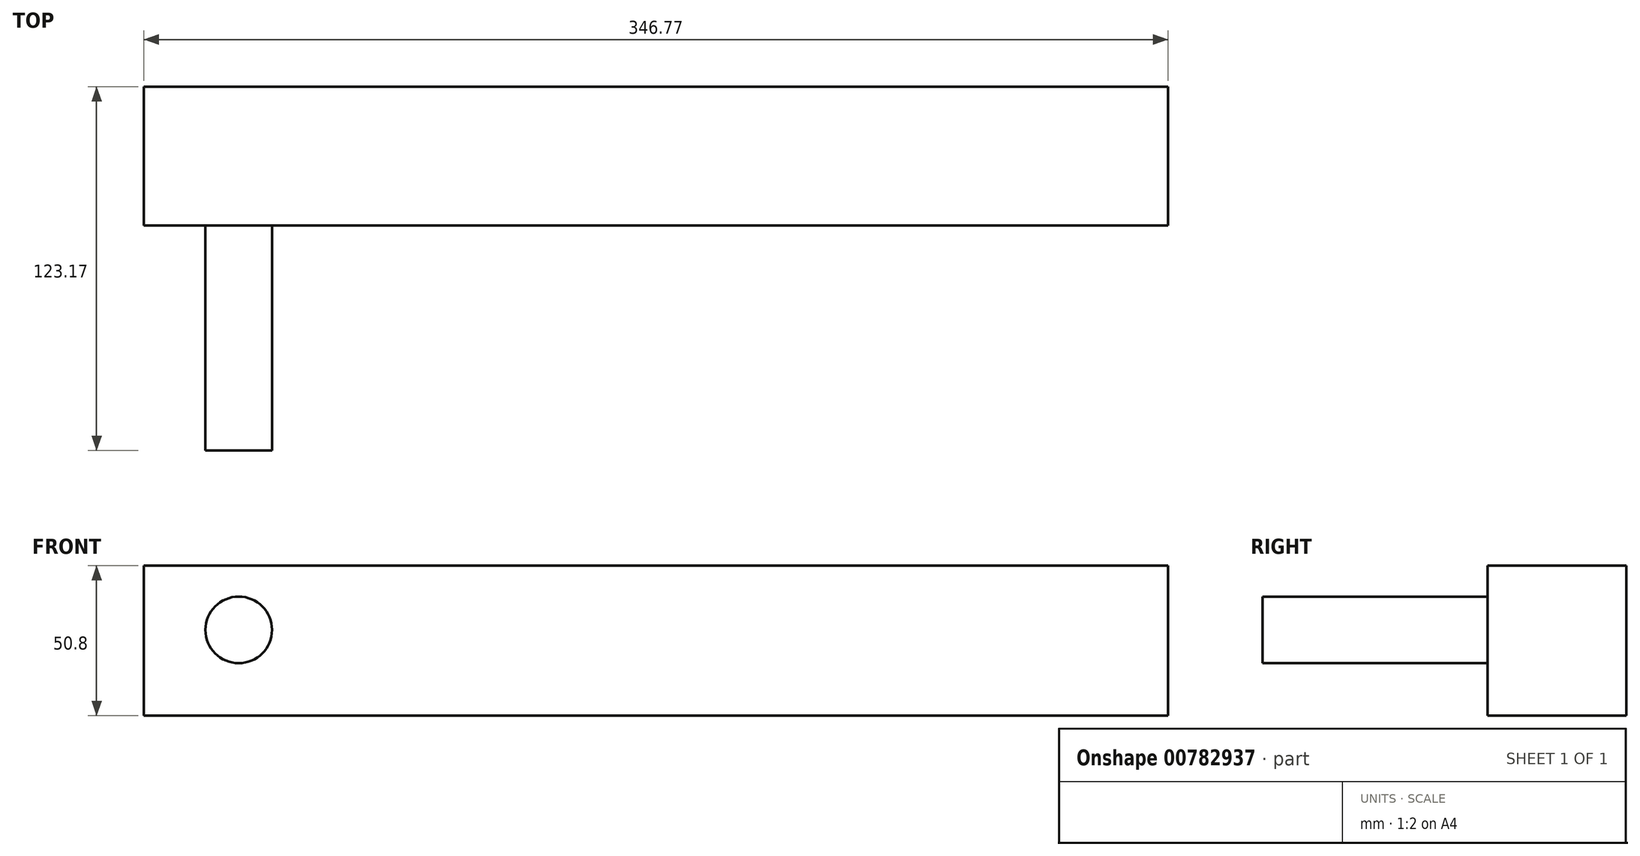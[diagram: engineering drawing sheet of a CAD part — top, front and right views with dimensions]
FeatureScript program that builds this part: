
annotation { "Feature Type Name" : "Feature", "Feature Type Description" : "" }
export const myFeature = defineFeature(function(context is Context, id is Id, definition is map)
    precondition{}
    {
        {
            var Q0;
            Q0=qCreatedBy(makeId("Top.planeOp"),FACE);
            var sketch = newSketch(context, id + "F0", { "sketchPlane" : qUnion([Q0])});
            skLineSegment(sketch, "E0.bottom", {"start": v(-140.56, 22.3) * mm, "end": v(206.2, 22.3) * mm});
            skLineSegment(sketch, "E0.top", {"start": v(-140.56, -24.68) * mm, "end": v(206.2, -24.68) * mm});
            skLineSegment(sketch, "E0.left", {"start": v(-140.56, 22.3) * mm, "end": v(-140.56, -24.68) * mm});
            skLineSegment(sketch, "E0.right", {"start": v(206.2, 22.3) * mm, "end": v(206.2, -24.68) * mm});
            skSolve(sketch);
        }
        {
            var Q0;
            Q0=makeQuery(id+"F0.imprint","IMPRINT",FACE,{"disambiguationData":[TD([[makeQuery(id+"F0.imprint","IMPRINT",EDGE,{"derivedFrom":sQuery(id+"F0.wireOp",EDGE,"E0.bottom")}),-1.0]])]});
            extrude(context, id + "F1", {"entities" : qUnion([Q0]), "surfaceOperationType" : NewSurfaceOperationType.ADD, "depth" : 50.8 * mm, "offsetDistance" : 25.4 * mm});
        }
        {
            var Q0;
            Q0=makeQuery(id+"F1.opExtrude","SWEPT_FACE",FACE,{"disambiguationData":[OSD([sQuery(id+"F0.wireOp",EDGE,"E0.top")])]});
            var sketch = newSketch(context, id + "F2", { "sketchPlane" : qUnion([Q0])});
            skCircle(sketch, "E1", {"center": v(-108.46, 29.02) * mm, "radius": 11.28 * mm});
            skSolve(sketch);
        }
        {
            var Q0;
            Q0=makeQuery(id+"F2.imprint","IMPRINT",FACE,{"disambiguationData":[TD([[makeQuery(id+"F2.imprint","IMPRINT",EDGE,{"derivedFrom":sQuery(id+"F2.wireOp",EDGE,"E1")}),1.0]])]});
            extrude(context, id + "F3", {"entities" : qUnion([Q0]), "operationType" : NewBodyOperationType.ADD, "depth" : 76.2 * mm, "offsetDistance" : 25.4 * mm});
        }
    });
